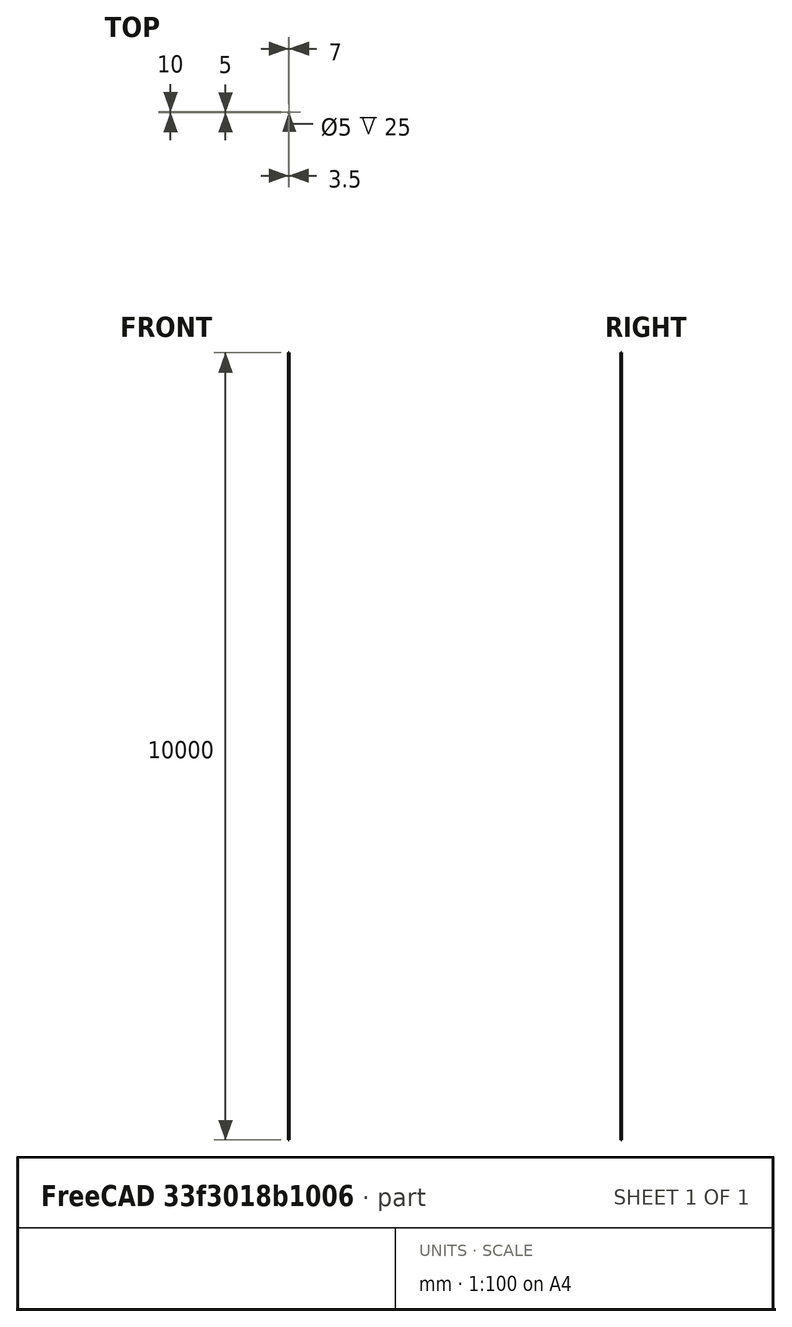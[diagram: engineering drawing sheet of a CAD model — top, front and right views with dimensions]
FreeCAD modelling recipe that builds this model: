
FCSTD DOCUMENT  (FreeCAD 0.16R6712 (Git))
Label: DOIGT_EXT
License: All rights reserved
LicenseURL: http://en.wikipedia.org/wiki/All_rights_reserved
objects: Sketcher::SketchObject×5, PartDesign::Pocket×3, PartDesign::Pad×2, Part::Torus×1, Part::Cut×1, Mesh::Feature×1
note: 17 computed .brp shape members not serialized (recipe doc carries the construction recipe); baked Part::Feature solids carry a one-line shape summary decoded from their .brp

FEATURE [Sketcher::SketchObject] Sketch
  sketch-geometry (1):
    g0: Circle CenterX=0 CenterY=0 CenterZ=0 NormalX=0 NormalY=0 NormalZ=1 Radius=3.5
  constraints (2):
    c: Coincident(g0,g-1)
    c: Radius(g0) = 3.5
FEATURE [PartDesign::Pad] Pad
  Length = 30
  Length2 = 100
  Sketch = -> Sketch
  Type = 0
FEATURE [Sketcher::SketchObject] Sketch001
  Placement = pos=(0,0,0) rot=(1,0,0;3.14159rad)
  Support = -> Pad [Face2]
  sketch-geometry (6):
    g0: LineSegment StartX=-2.5 StartY=5 StartZ=0 EndX=2.5 EndY=5 EndZ=0
    g1: LineSegment StartX=2.5 StartY=5 StartZ=0 EndX=2.5 EndY=-5 EndZ=0
    g2: LineSegment StartX=2.5 StartY=-5 StartZ=0 EndX=-2.5 EndY=-5 EndZ=0
    g3: LineSegment StartX=-2.5 StartY=-5 StartZ=0 EndX=-2.5 EndY=5 EndZ=0
    g4: LineSegment [constr] StartX=0 StartY=0 StartZ=0 EndX=-2.5 EndY=0 EndZ=0
    g5: LineSegment [constr] StartX=0 StartY=0 StartZ=0 EndX=2.5 EndY=0 EndZ=0
  constraints (14):
    c: Coincident(g0,g1)
    c: Coincident(g1,g2)
    c: Coincident(g2,g3)
    c: Coincident(g3,g0)
    c: Horizontal(g0)
    c: Horizontal(g2)
    c: Vertical(g1)
    c: Vertical(g3)
    c: Coincident(g4,g-1)
    c: PointOnObject(g4,g3)
    c: Horizontal(g4)
    c: Coincident(g5,g-1)
    c: Horizontal(g5)
    c: Distance(g4) = 2.5
FEATURE [PartDesign::Pocket] Pocket
  Length = 5
  Sketch = -> Sketch001
  Type = 0
FEATURE [Sketcher::SketchObject] Sketch002
  Placement = pos=(0,0,30) rot=(0,0,1;0rad)
  Support = -> Pocket [Face7]
  sketch-geometry (1):
    g0: Circle CenterX=0 CenterY=0 CenterZ=0 NormalX=0 NormalY=0 NormalZ=1 Radius=2.5
  constraints (2):
    c: Coincident(g0,g-1)
    c: Radius(g0) = 2.5
FEATURE [PartDesign::Pocket] Pocket001
  Length = 5
  Sketch = -> Sketch002
  Type = 1
FEATURE [Sketcher::SketchObject] Sketch003
  Placement = pos=(0,0,30) rot=(0,0,1;0rad)
  Support = -> Pocket001 [Face10]
  sketch-geometry (8):
    g0: LineSegment StartX=-1 StartY=-1.67736 StartZ=0 EndX=1 EndY=-1.67736 EndZ=0
    g1: LineSegment StartX=1 StartY=-1.67736 StartZ=0 EndX=1 EndY=-4.15853 EndZ=0
    g2: LineSegment StartX=1 StartY=-4.15853 StartZ=0 EndX=-1 EndY=-4.15853 EndZ=0
    g3: LineSegment StartX=-1 StartY=-4.15853 StartZ=0 EndX=-1 EndY=-1.67736 EndZ=0
    g4: LineSegment [constr] StartX=-1 StartY=-4.15853 StartZ=0 EndX=1 EndY=-1.67736 EndZ=0
    g5: LineSegment [constr] StartX=-1 StartY=-1.67736 StartZ=0 EndX=1 EndY=-4.15853 EndZ=0
    g6: GeomPoint [constr] X=0 Y=-2.91795 Z=0
    g7: GeomPoint [constr] X=0 Y=-2.91795 Z=0
  constraints (17):
    c: Coincident(g0,g1)
    c: Coincident(g1,g2)
    c: Coincident(g2,g3)
    c: Coincident(g3,g0)
    c: Horizontal(g0)
    c: Horizontal(g2)
    c: Vertical(g1)
    c: Vertical(g3)
    c: DistanceX(g0,g0) = 2
    c: Coincident(g4,g2)
    c: Coincident(g4,g0)
    c: Coincident(g5,g0)
    c: Coincident(g5,g1)
    c: PointOnObject(g6,g5)
    c: PointOnObject(g7,g4)
    c: Coincident(g6,g7)
    c: PointOnObject(g6,g-2)
FEATURE [PartDesign::Pocket] Pocket003
  Length = 10
  Sketch = -> Sketch003
  Type = 0
FEATURE [Sketcher::SketchObject] Sketch004
  Placement = pos=(0,0,30) rot=(0,0,1;0rad)
  Support = -> Pocket003 [Face2]
  sketch-geometry (1):
    g0: Circle CenterX=0 CenterY=0 CenterZ=0 NormalX=0 NormalY=0 NormalZ=1 Radius=2.4
  constraints (2):
    c: Coincident(g0,g-1)
    c: Radius(g0) = 2.4
FEATURE [PartDesign::Pad] Pad001
  Length = 40
  Length2 = 100
  Sketch = -> Sketch004
  Type = 0
FEATURE [Part::Torus] Torus  label="Tore"
  Angle1 = -180
  Angle2 = 180
  Angle3 = 360
  Placement = pos=(0,0,30) rot=(0,0,1;0rad)
  Radius1 = 3
  Radius2 = 0.2
FEATURE [Part::Cut] Cut
  Base = -> Pad001
  Tool = -> Torus
FEATURE [Mesh::Feature] Mesh  label="Cut (Meshed)"
